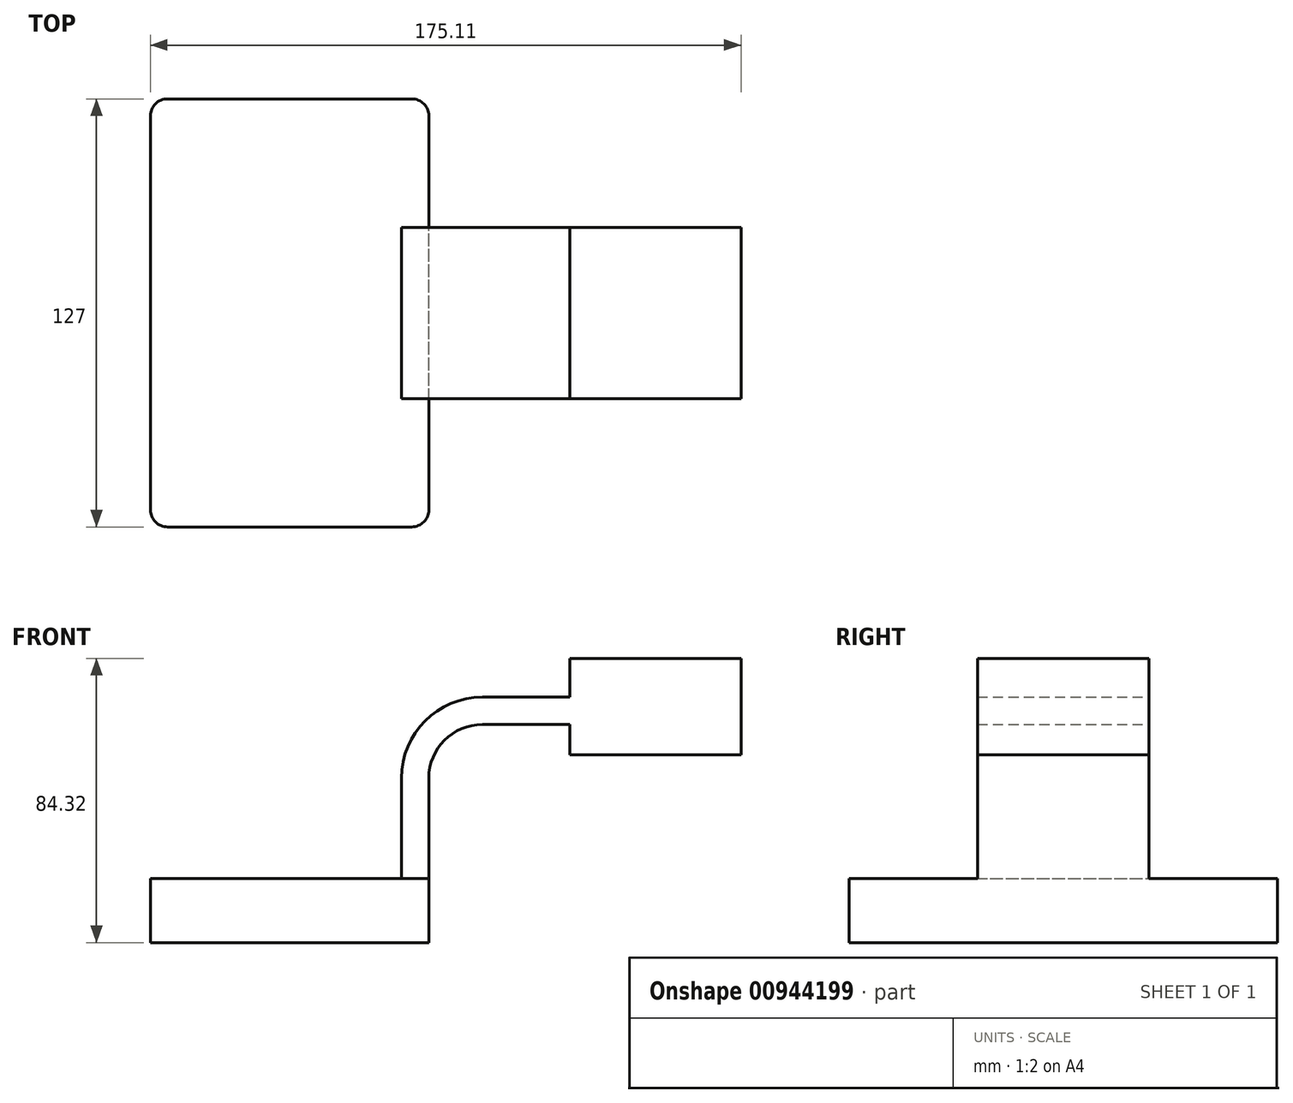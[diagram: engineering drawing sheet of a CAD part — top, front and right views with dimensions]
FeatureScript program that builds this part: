
annotation { "Feature Type Name" : "Feature", "Feature Type Description" : "" }
export const myFeature = defineFeature(function(context is Context, id is Id, definition is map)
    precondition{}
    {
        {
            var Q0;
            Q0=qCreatedBy(makeId("Front.planeOp"),FACE);
            var sketch = newSketch(context, id + "F0", { "sketchPlane" : qUnion([Q0])});
            skLineSegment(sketch, "E0.bottom", {"start": v(41.27, 9.53) * mm, "end": v(-41.28, 9.53) * mm});
            skLineSegment(sketch, "E0.top", {"start": v(41.28, -9.52) * mm, "end": v(-41.27, -9.52) * mm});
            skLineSegment(sketch, "E0.left", {"start": v(41.28, 9.53) * mm, "end": v(41.28, -9.52) * mm});
            skLineSegment(sketch, "E0.right", {"start": v(-41.28, 9.53) * mm, "end": v(-41.27, -9.52) * mm});
            skPoint(sketch, "E0.middle", {"position": v(0, 0) * mm});
            skLineSegment(sketch, "E1.bottom", {"start": v(83.04, 74.79) * mm, "end": v(133.84, 74.79) * mm});
            skLineSegment(sketch, "E1.top", {"start": v(83.04, 46.21) * mm, "end": v(133.84, 46.21) * mm});
            skLineSegment(sketch, "E1.left", {"start": v(83.04, 74.79) * mm, "end": v(83.04, 46.21) * mm});
            skLineSegment(sketch, "E1.right", {"start": v(133.84, 74.79) * mm, "end": v(133.84, 46.21) * mm});
            skPoint(sketch, "E1.middle", {"position": v(108.44, 60.5) * mm});
            skLineSegment(sketch, "E2", {"start": v(41.27, 9.53) * mm, "end": v(41.27, 39.27) * mm});
            skArc(sketch, "E3", {"start": v(41.27, 39.27) * mm, "mid": v(45.92, 50.5) * mm, "end": v(57.15, 55.15) * mm});
            skLineSegment(sketch, "E4", {"start": v(57.15, 55.15) * mm, "end": v(98.4, 55.15) * mm});
            skLineSegment(sketch, "E5.0", {"start": v(57.15, 63.27) * mm, "end": v(98.4, 63.27) * mm});
            skArc(sketch, "E5.1", {"start": v(33.15, 39.27) * mm, "mid": v(40.18, 56.24) * mm, "end": v(57.15, 63.27) * mm});
            skLineSegment(sketch, "E5.2", {"start": v(33.15, 9.53) * mm, "end": v(33.15, 39.27) * mm});
            skFitSpline(sketch, "E6", {"points": [v(-41.28, 9.52) * mm, v(83.04, 74.79) * mm], "startDerivative": vector(91.87, 178.45) * mm, "endDerivative": vector(120.5, 22.24) * mm});
            skSolve(sketch);
        }
        {
            var Q0;
            Q0=makeQuery(id+"F0.imprint","IMPRINT",FACE,{"disambiguationData":[TD([[makeQuery(id+"F0.imprint","IMPRINT",EDGE,{"derivedFrom":sQuery(id+"F0.wireOp",EDGE,"E0.top")}),-1.0]])]});
            extrude(context, id + "F1", {"entities" : qUnion([Q0]), "endBound" : BoundingType.SYMMETRIC, "depth" : 127 * mm, "offsetDistance" : 25.4 * mm});
        }
        {
            var Q0;
            {var subQ1=sQuery(id+"F0.wireOp",EDGE,"E2");Q0=makeQuery(id+"F0.imprint","IMPRINT",FACE,{"disambiguationData":[TD([[makeQuery(id+"F0.imprint","IMPRINT",EDGE,{"derivedFrom":subQ1}),1.0]])]});}
            var Q1;
            {var subQ3=sQuery(id+"F0.wireOp",EDGE,"E1.bottom");Q1=makeQuery(id+"F0.imprint","IMPRINT",FACE,{"disambiguationData":[TD([[makeQuery(id+"F0.imprint","IMPRINT",EDGE,{"derivedFrom":subQ3}),-1.0]])]});}
            extrude(context, id + "F2", {"entities" : qUnion([Q0, Q1]), "operationType" : NewBodyOperationType.ADD, "endBound" : BoundingType.SYMMETRIC, "depth" : 50.8 * mm, "offsetDistance" : 25.4 * mm});
        }
        {
            var Q0;
            {var subQ0=sQuery(id+"F0.wireOp",EDGE,"E5.1");Q0=makeQuery(id+"F0.imprint","IMPRINT",FACE,{"disambiguationData":[TD([[makeQuery(id+"F0.imprint","IMPRINT",EDGE,{"derivedFrom":subQ0}),1.0]])]});}
            extrude(context, id + "F3", {"entities" : qUnion([Q0]), "operationType" : NewBodyOperationType.ADD, "endBound" : BoundingType.SYMMETRIC, "depth" : 15.88 * mm, "offsetDistance" : 25.4 * mm});
        }
        {
            var Q0;
            Q0=makeQuery(id+"F1.opExtrude","CAP_EDGE",EDGE,{"disambiguationData":[OSD([sQuery(id+"F0.wireOp",EDGE,"E0.right")])],"isStart":false});
            var Q1;
            Q1=makeQuery(id+"F1.opExtrude","CAP_EDGE",EDGE,{"disambiguationData":[OSD([sQuery(id+"F0.wireOp",EDGE,"E0.left")])],"isStart":false});
            var Q2;
            Q2=makeQuery(id+"F1.opExtrude","CAP_EDGE",EDGE,{"disambiguationData":[OSD([sQuery(id+"F0.wireOp",EDGE,"E0.left")])],"isStart":true});
            var Q3;
            Q3=makeQuery(id+"F1.opExtrude","CAP_EDGE",EDGE,{"disambiguationData":[OSD([sQuery(id+"F0.wireOp",EDGE,"E0.right")])],"isStart":true});
            fillet(context, id + "F4", {"entities" : qUnion([Q0, Q1, Q2, Q3]), "radius" : 5.08 * mm, "tangentPropagation" : true, "allowEdgeOverflow" : false});
        }
    });
